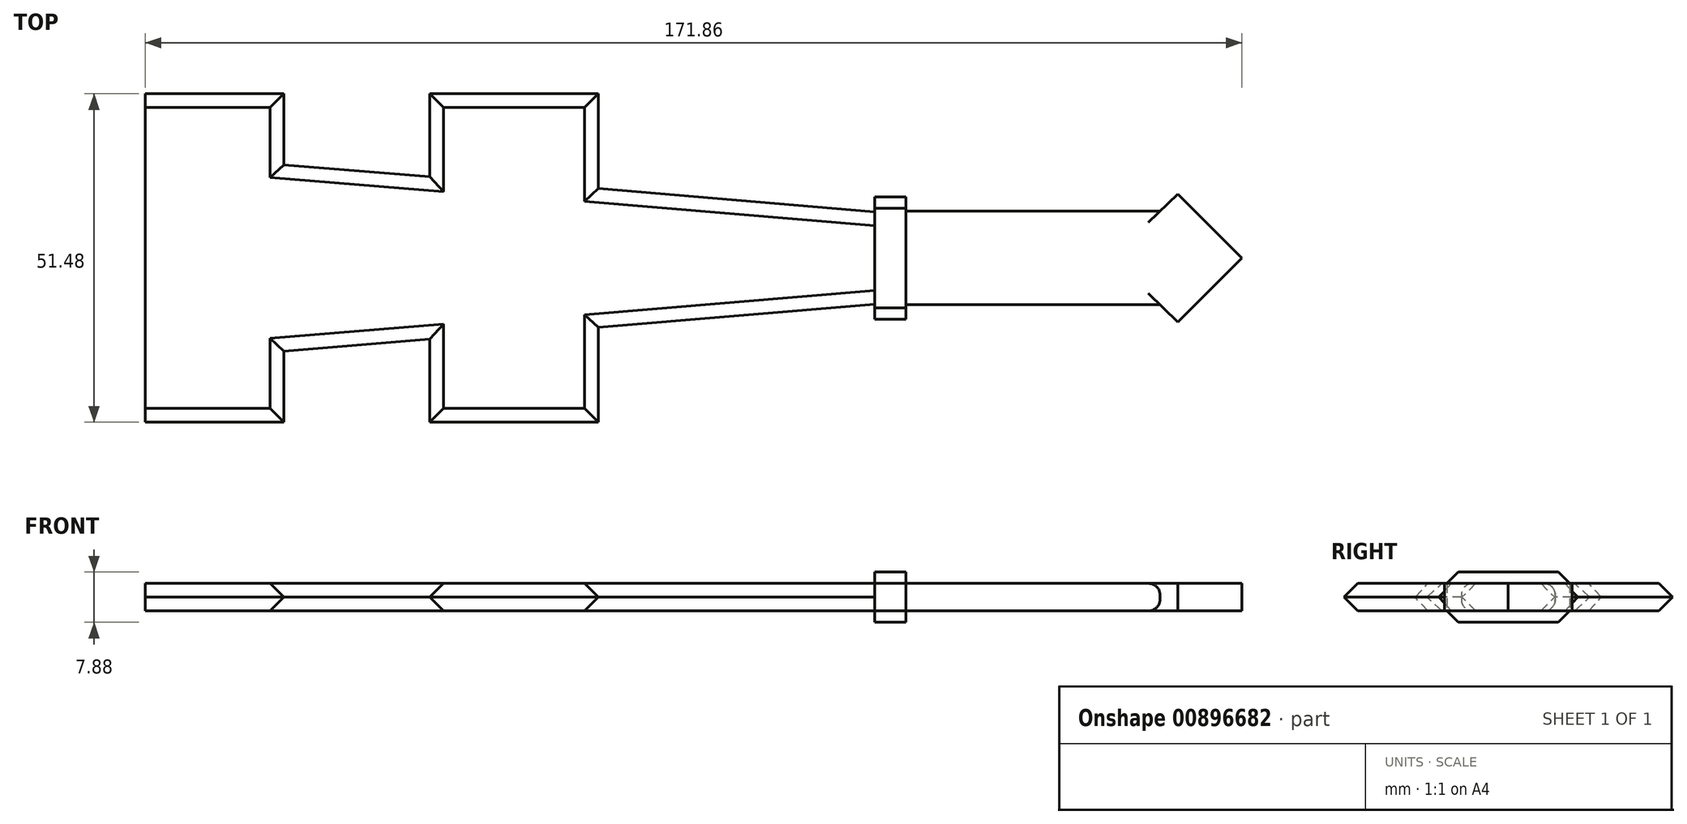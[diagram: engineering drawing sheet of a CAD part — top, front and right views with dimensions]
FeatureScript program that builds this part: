
annotation { "Feature Type Name" : "Feature", "Feature Type Description" : "" }
export const myFeature = defineFeature(function(context is Context, id is Id, definition is map)
    precondition{}
    {
        {
            var Q0;
            Q0=qCreatedBy(makeId("Top.planeOp"),FACE);
            var sketch = newSketch(context, id + "F0", { "sketchPlane" : qUnion([Q0])});
            skLineSegment(sketch, "E0", {"start": v(-86.75, 19.78) * mm, "end": v(-86.75, -31.7) * mm});
            skLineSegment(sketch, "E1", {"start": v(-86.75, -31.7) * mm, "end": v(-64.99, -31.7) * mm});
            skLineSegment(sketch, "E2", {"start": v(-64.99, -31.7) * mm, "end": v(-64.99, -20.56) * mm});
            skLineSegment(sketch, "E3", {"start": v(-64.99, -20.56) * mm, "end": v(-42.16, -18.7) * mm});
            skLineSegment(sketch, "E4", {"start": v(-42.16, -18.7) * mm, "end": v(-42.16, -31.7) * mm});
            skLineSegment(sketch, "E5", {"start": v(-42.16, -31.7) * mm, "end": v(-15.76, -31.7) * mm});
            skLineSegment(sketch, "E6", {"start": v(-15.76, -31.7) * mm, "end": v(-15.76, -16.84) * mm});
            skLineSegment(sketch, "E7", {"start": v(-15.76, -16.84) * mm, "end": v(27.57, -13.22) * mm});
            skLineSegment(sketch, "E8", {"start": v(27.57, -13.22) * mm, "end": v(27.57, -15.56) * mm});
            skLineSegment(sketch, "E9", {"start": v(27.57, -15.56) * mm, "end": v(32.43, -15.56) * mm});
            skLineSegment(sketch, "E10", {"start": v(32.43, -13.32) * mm, "end": v(72.28, -13.32) * mm});
            skLineSegment(sketch, "E11", {"start": v(72.28, -13.32) * mm, "end": v(75.04, -16) * mm});
            skLineSegment(sketch, "E12", {"start": v(85.1, -5.97) * mm, "end": v(75.04, -16) * mm});
            skLineSegment(sketch, "E13.MirrorCS", {"start": v(72.28, 1.38) * mm, "end": v(75.04, 4.06) * mm});
            skLineSegment(sketch, "E14.MirrorCS", {"start": v(27.57, 1.29) * mm, "end": v(27.57, 3.63) * mm});
            skLineSegment(sketch, "E15.MirrorCS", {"start": v(-15.76, 4.9) * mm, "end": v(27.57, 1.29) * mm});
            skLineSegment(sketch, "E16.MirrorCS", {"start": v(32.43, 1.38) * mm, "end": v(72.28, 1.38) * mm});
            skLineSegment(sketch, "E17.MirrorCS", {"start": v(27.57, 3.63) * mm, "end": v(32.43, 3.63) * mm});
            skLineSegment(sketch, "E18.MirrorCS", {"start": v(85.1, -5.97) * mm, "end": v(75.04, 4.06) * mm});
            skLineSegment(sketch, "E19.MirrorCS", {"start": v(-42.16, 6.77) * mm, "end": v(-42.16, 19.77) * mm});
            skLineSegment(sketch, "E20.MirrorCS", {"start": v(-64.99, 8.63) * mm, "end": v(-42.16, 6.77) * mm});
            skLineSegment(sketch, "E21.MirrorCS", {"start": v(-15.76, 19.77) * mm, "end": v(-15.76, 4.9) * mm});
            skLineSegment(sketch, "E22.MirrorCS", {"start": v(-42.16, 19.77) * mm, "end": v(-15.76, 19.77) * mm});
            skLineSegment(sketch, "E23.MirrorCS", {"start": v(-86.75, 19.77) * mm, "end": v(-64.99, 19.77) * mm});
            skLineSegment(sketch, "E24.MirrorCS", {"start": v(-64.99, 19.77) * mm, "end": v(-64.99, 8.63) * mm});
            skLineSegment(sketch, "E25.MirrorCS", {"start": v(-86.75, -31.72) * mm, "end": v(-86.75, 19.77) * mm});
            skLineSegment(sketch, "E26", {"start": v(32.43, -15.56) * mm, "end": v(32.43, -13.32) * mm});
            skLineSegment(sketch, "E27", {"start": v(32.43, 1.38) * mm, "end": v(32.43, 3.63) * mm});
            skLineSegment(sketch, "E28", {"start": v(27.57, 1.29) * mm, "end": v(27.57, -13.22) * mm});
            skLineSegment(sketch, "E29", {"start": v(32.43, -13.32) * mm, "end": v(32.43, 1.38) * mm});
            skSolve(sketch);
        }
        {
            var Q0;
            Q0=qCreatedBy(makeId("Top.planeOp"),FACE);
            var sketch = newSketch(context, id + "F1", { "sketchPlane" : qUnion([Q0])});
            skSolve(sketch);
        }
        {
            var Q0;
            Q0 = qSketchRegion(id + "F1", true);
            var Q1;
            Q1=makeQuery(id+"F0.imprint","IMPRINT",FACE,{"disambiguationData":[TD([[makeQuery(id+"F0.imprint","IMPRINT",EDGE,{"derivedFrom":sQuery(id+"F0.wireOp",EDGE,"E8")}),1.0]])]});
            var Q2;
            Q2=makeQuery(id+"F0.imprint","IMPRINT",FACE,{"disambiguationData":[TD([[makeQuery(id+"F0.imprint","IMPRINT",EDGE,{"derivedFrom":sQuery(id+"F0.wireOp",EDGE,"E10")}),1.0]])]});
            var Q3;
            {var subQ0=sQuery(id+"F0.wireOp",EDGE,"E1");Q3=makeQuery(id+"F0.imprint","IMPRINT",FACE,{"disambiguationData":[TD([[makeQuery(id+"F0.imprint","IMPRINT",EDGE,{"derivedFrom":subQ0}),1.0]])]});}
            extrude(context, id + "F2", {"entities" : qUnion([Q0, Q1, Q2, Q3]), "depth" : 4.32 * mm, "offsetDistance" : 25.4 * mm});
        }
        {
            var Q0;
            Q0=makeQuery(id+"F2.opExtrude","CAP_EDGE",EDGE,{"disambiguationData":[OSD([sQuery(id+"F0.wireOp",EDGE,"E3")])],"isStart":false});
            var Q1;
            Q1=makeQuery(id+"F2.opExtrude","CAP_EDGE",EDGE,{"disambiguationData":[OSD([sQuery(id+"F0.wireOp",EDGE,"E4")])],"isStart":false});
            var Q2;
            Q2=makeQuery(id+"F2.opExtrude","CAP_EDGE",EDGE,{"disambiguationData":[OSD([sQuery(id+"F0.wireOp",EDGE,"E5")])],"isStart":false});
            var Q3;
            Q3=makeQuery(id+"F2.opExtrude","CAP_EDGE",EDGE,{"disambiguationData":[OSD([sQuery(id+"F0.wireOp",EDGE,"E6")])],"isStart":false});
            var Q4;
            Q4=makeQuery(id+"F2.opExtrude","CAP_EDGE",EDGE,{"disambiguationData":[OSD([sQuery(id+"F0.wireOp",EDGE,"E7")])],"isStart":false});
            var Q5;
            Q5=makeQuery(id+"F2.opExtrude","CAP_EDGE",EDGE,{"disambiguationData":[OSD([sQuery(id+"F0.wireOp",EDGE,"E15.MirrorCS")])],"isStart":false});
            var Q6;
            Q6=makeQuery(id+"F2.opExtrude","CAP_EDGE",EDGE,{"disambiguationData":[OSD([sQuery(id+"F0.wireOp",EDGE,"E21.MirrorCS")])],"isStart":false});
            var Q7;
            Q7=makeQuery(id+"F2.opExtrude","CAP_EDGE",EDGE,{"disambiguationData":[OSD([sQuery(id+"F0.wireOp",EDGE,"E22.MirrorCS")])],"isStart":false});
            var Q8;
            Q8=makeQuery(id+"F2.opExtrude","CAP_EDGE",EDGE,{"disambiguationData":[OSD([sQuery(id+"F0.wireOp",EDGE,"E19.MirrorCS")])],"isStart":false});
            var Q9;
            Q9=makeQuery(id+"F2.opExtrude","CAP_EDGE",EDGE,{"disambiguationData":[OSD([sQuery(id+"F0.wireOp",EDGE,"E20.MirrorCS")])],"isStart":false});
            var Q10;
            Q10=makeQuery(id+"F2.opExtrude","CAP_EDGE",EDGE,{"disambiguationData":[OSD([sQuery(id+"F0.wireOp",EDGE,"E24.MirrorCS")])],"isStart":false});
            var Q11;
            Q11=makeQuery(id+"F2.opExtrude","CAP_EDGE",EDGE,{"disambiguationData":[OSD([sQuery(id+"F0.wireOp",EDGE,"E23.MirrorCS")])],"isStart":false});
            var Q12;
            Q12=makeQuery(id+"F2.opExtrude","CAP_EDGE",EDGE,{"disambiguationData":[OSD([sQuery(id+"F0.wireOp",EDGE,"E25.MirrorCS")])],"isStart":false});
            var Q13;
            Q13=makeQuery(id+"F2.opExtrude","CAP_EDGE",EDGE,{"disambiguationData":[OSD([sQuery(id+"F0.wireOp",EDGE,"E1")])],"isStart":false});
            var Q14;
            Q14=makeQuery(id+"F2.opExtrude","CAP_EDGE",EDGE,{"disambiguationData":[OSD([sQuery(id+"F0.wireOp",EDGE,"E2")])],"isStart":false});
            var Q15;
            Q15=makeQuery(id+"F2.opExtrude","CAP_EDGE",EDGE,{"disambiguationData":[OSD([sQuery(id+"F0.wireOp",EDGE,"E5")])],"isStart":true});
            var Q16;
            Q16=makeQuery(id+"F2.opExtrude","CAP_EDGE",EDGE,{"disambiguationData":[OSD([sQuery(id+"F0.wireOp",EDGE,"E6")])],"isStart":true});
            var Q17;
            Q17=makeQuery(id+"F2.opExtrude","CAP_EDGE",EDGE,{"disambiguationData":[OSD([sQuery(id+"F0.wireOp",EDGE,"E7")])],"isStart":true});
            var Q18;
            Q18=makeQuery(id+"F2.opExtrude","CAP_EDGE",EDGE,{"disambiguationData":[OSD([sQuery(id+"F0.wireOp",EDGE,"E4")])],"isStart":true});
            var Q19;
            Q19=makeQuery(id+"F2.opExtrude","CAP_EDGE",EDGE,{"disambiguationData":[OSD([sQuery(id+"F0.wireOp",EDGE,"E3")])],"isStart":true});
            var Q20;
            Q20=makeQuery(id+"F2.opExtrude","CAP_EDGE",EDGE,{"disambiguationData":[OSD([sQuery(id+"F0.wireOp",EDGE,"E1")])],"isStart":true});
            var Q21;
            Q21=makeQuery(id+"F2.opExtrude","CAP_EDGE",EDGE,{"disambiguationData":[OSD([sQuery(id+"F0.wireOp",EDGE,"E2")])],"isStart":true});
            var Q22;
            Q22=makeQuery(id+"F2.opExtrude","CAP_EDGE",EDGE,{"disambiguationData":[OSD([sQuery(id+"F0.wireOp",EDGE,"E25.MirrorCS")])],"isStart":true});
            var Q23;
            Q23=makeQuery(id+"F2.opExtrude","CAP_EDGE",EDGE,{"disambiguationData":[OSD([sQuery(id+"F0.wireOp",EDGE,"E23.MirrorCS")])],"isStart":true});
            var Q24;
            Q24=makeQuery(id+"F2.opExtrude","CAP_EDGE",EDGE,{"disambiguationData":[OSD([sQuery(id+"F0.wireOp",EDGE,"E24.MirrorCS")])],"isStart":true});
            var Q25;
            Q25=makeQuery(id+"F2.opExtrude","CAP_EDGE",EDGE,{"disambiguationData":[OSD([sQuery(id+"F0.wireOp",EDGE,"E20.MirrorCS")])],"isStart":true});
            var Q26;
            Q26=makeQuery(id+"F2.opExtrude","CAP_EDGE",EDGE,{"disambiguationData":[OSD([sQuery(id+"F0.wireOp",EDGE,"E21.MirrorCS")])],"isStart":true});
            var Q27;
            Q27=makeQuery(id+"F2.opExtrude","CAP_EDGE",EDGE,{"disambiguationData":[OSD([sQuery(id+"F0.wireOp",EDGE,"E15.MirrorCS")])],"isStart":true});
            var Q28;
            Q28=makeQuery(id+"F2.opExtrude","CAP_EDGE",EDGE,{"disambiguationData":[OSD([sQuery(id+"F0.wireOp",EDGE,"E19.MirrorCS")])],"isStart":true});
            var Q29;
            Q29=makeQuery(id+"F2.opExtrude","CAP_EDGE",EDGE,{"disambiguationData":[OSD([sQuery(id+"F0.wireOp",EDGE,"E22.MirrorCS")])],"isStart":true});
            chamfer(context, id + "F3", {"entities" : qUnion([Q0, Q1, Q2, Q3, Q4, Q5, Q6, Q7, Q8, Q9, Q10, Q11, Q12, Q13, Q14, Q15, Q16, Q17, Q18, Q19, Q20, Q21, Q22, Q23, Q24, Q25, Q26, Q27, Q28, Q29]), "width" : 2.16 * mm, "tangentPropagation" : true});
        }
        {
            var Q0;
            Q0=makeQuery(id+"F2.opExtrude","CAP_FACE",FACE,{"disambiguationData":[OSD([sQuery(id+"F0.wireOp",EDGE,"E1"),sQuery(id+"F0.wireOp",EDGE,"E2"),sQuery(id+"F0.wireOp",EDGE,"E3"),sQuery(id+"F0.wireOp",EDGE,"E4"),sQuery(id+"F0.wireOp",EDGE,"E5"),sQuery(id+"F0.wireOp",EDGE,"E6"),sQuery(id+"F0.wireOp",EDGE,"E7"),sQuery(id+"F0.wireOp",EDGE,"E8"),sQuery(id+"F0.wireOp",EDGE,"E9"),sQuery(id+"F0.wireOp",EDGE,"E10"),sQuery(id+"F0.wireOp",EDGE,"E11"),sQuery(id+"F0.wireOp",EDGE,"E12"),sQuery(id+"F0.wireOp",EDGE,"E13.MirrorCS"),sQuery(id+"F0.wireOp",EDGE,"E14.MirrorCS"),sQuery(id+"F0.wireOp",EDGE,"E15.MirrorCS"),sQuery(id+"F0.wireOp",EDGE,"E16.MirrorCS"),sQuery(id+"F0.wireOp",EDGE,"E17.MirrorCS"),sQuery(id+"F0.wireOp",EDGE,"E18.MirrorCS"),sQuery(id+"F0.wireOp",EDGE,"E19.MirrorCS"),sQuery(id+"F0.wireOp",EDGE,"E21.MirrorCS"),sQuery(id+"F0.wireOp",EDGE,"E22.MirrorCS"),sQuery(id+"F0.wireOp",EDGE,"E20.MirrorCS"),sQuery(id+"F0.wireOp",EDGE,"E23.MirrorCS"),sQuery(id+"F0.wireOp",EDGE,"E24.MirrorCS"),sQuery(id+"F0.wireOp",EDGE,"E25.MirrorCS"),sQuery(id+"F0.wireOp",EDGE,"E26"),sQuery(id+"F0.wireOp",EDGE,"E27")])],"isStart":false});
            var sketch = newSketch(context, id + "F4", { "sketchPlane" : qUnion([Q0])});
            skLineSegment(sketch, "E30", {"start": v(27.57, 3.63) * mm, "end": v(27.57, -15.56) * mm});
            skLineSegment(sketch, "E31", {"start": v(27.57, -15.56) * mm, "end": v(32.43, -15.56) * mm});
            skLineSegment(sketch, "E32", {"start": v(32.43, -15.56) * mm, "end": v(32.43, 3.63) * mm});
            skLineSegment(sketch, "E33", {"start": v(32.43, 3.63) * mm, "end": v(27.57, 3.63) * mm});
            skSolve(sketch);
        }
        {
            var Q0;
            {var subQ0=sQuery(id+"F4.wireOp",EDGE,"E31");Q0=makeQuery(id+"F4.imprint","IMPRINT",FACE,{"disambiguationData":[TD([[makeQuery(id+"F4.imprint","IMPRINT",EDGE,{"derivedFrom":subQ0}),1.0]])]});}
            extrude(context, id + "F5", {"entities" : qUnion([Q0]), "operationType" : NewBodyOperationType.ADD, "depth" : 1.78 * mm, "offsetDistance" : 25.4 * mm});
        }
        {
            var Q0;
            Q0=makeQuery(id+"F2.opExtrude","CAP_FACE",FACE,{"disambiguationData":[OSD([sQuery(id+"F0.wireOp",EDGE,"E1"),sQuery(id+"F0.wireOp",EDGE,"E2"),sQuery(id+"F0.wireOp",EDGE,"E3"),sQuery(id+"F0.wireOp",EDGE,"E4"),sQuery(id+"F0.wireOp",EDGE,"E5"),sQuery(id+"F0.wireOp",EDGE,"E6"),sQuery(id+"F0.wireOp",EDGE,"E7"),sQuery(id+"F0.wireOp",EDGE,"E8"),sQuery(id+"F0.wireOp",EDGE,"E9"),sQuery(id+"F0.wireOp",EDGE,"E10"),sQuery(id+"F0.wireOp",EDGE,"E11"),sQuery(id+"F0.wireOp",EDGE,"E12"),sQuery(id+"F0.wireOp",EDGE,"E13.MirrorCS"),sQuery(id+"F0.wireOp",EDGE,"E14.MirrorCS"),sQuery(id+"F0.wireOp",EDGE,"E15.MirrorCS"),sQuery(id+"F0.wireOp",EDGE,"E16.MirrorCS"),sQuery(id+"F0.wireOp",EDGE,"E17.MirrorCS"),sQuery(id+"F0.wireOp",EDGE,"E18.MirrorCS"),sQuery(id+"F0.wireOp",EDGE,"E19.MirrorCS"),sQuery(id+"F0.wireOp",EDGE,"E21.MirrorCS"),sQuery(id+"F0.wireOp",EDGE,"E22.MirrorCS"),sQuery(id+"F0.wireOp",EDGE,"E20.MirrorCS"),sQuery(id+"F0.wireOp",EDGE,"E23.MirrorCS"),sQuery(id+"F0.wireOp",EDGE,"E24.MirrorCS"),sQuery(id+"F0.wireOp",EDGE,"E25.MirrorCS"),sQuery(id+"F0.wireOp",EDGE,"E26"),sQuery(id+"F0.wireOp",EDGE,"E27")])],"isStart":true});
            var sketch = newSketch(context, id + "F6", { "sketchPlane" : qUnion([Q0])});
            skLineSegment(sketch, "E34", {"start": v(27.57, 15.56) * mm, "end": v(27.57, -3.63) * mm});
            skLineSegment(sketch, "E35", {"start": v(27.57, -3.63) * mm, "end": v(32.43, -3.63) * mm});
            skLineSegment(sketch, "E36", {"start": v(32.43, -3.63) * mm, "end": v(32.43, 15.56) * mm});
            skLineSegment(sketch, "E37", {"start": v(32.43, 15.56) * mm, "end": v(27.57, 15.56) * mm});
            skSolve(sketch);
        }
        {
            var Q0;
            {var subQ0=sQuery(id+"F6.wireOp",EDGE,"E35");Q0=makeQuery(id+"F6.imprint","IMPRINT",FACE,{"disambiguationData":[TD([[makeQuery(id+"F6.imprint","IMPRINT",EDGE,{"derivedFrom":subQ0}),1.0]])]});}
            extrude(context, id + "F7", {"entities" : qUnion([Q0]), "operationType" : NewBodyOperationType.ADD, "depth" : 1.78 * mm, "offsetDistance" : 25.4 * mm});
        }
        {
            var Q0;
            Q0=makeQuery(id+"F2.opExtrude","CAP_EDGE",EDGE,{"disambiguationData":[OSD([sQuery(id+"F0.wireOp",EDGE,"E16.MirrorCS")])],"isStart":true});
            var Q1;
            Q1=makeQuery(id+"F2.opExtrude","CAP_EDGE",EDGE,{"disambiguationData":[OSD([sQuery(id+"F0.wireOp",EDGE,"E10")])],"isStart":true});
            var Q2;
            Q2=makeQuery(id+"F2.opExtrude","CAP_EDGE",EDGE,{"disambiguationData":[OSD([sQuery(id+"F0.wireOp",EDGE,"E16.MirrorCS")])],"isStart":false});
            var Q3;
            Q3=makeQuery(id+"F2.opExtrude","CAP_EDGE",EDGE,{"disambiguationData":[OSD([sQuery(id+"F0.wireOp",EDGE,"E10")])],"isStart":false});
            fillet(context, id + "F8", {"entities" : qUnion([Q0, Q1, Q2, Q3]), "radius" : 1.78 * mm, "tangentPropagation" : true, "allowEdgeOverflow" : false});
        }
        {
            var Q0;
            Q0=makeQuery(id+"F7.opExtrude","CAP_EDGE",EDGE,{"disambiguationData":[OSD([sQuery(id+"F6.wireOp",EDGE,"E37")])],"isStart":false});
            var Q1;
            Q1=makeQuery(id+"F5.opExtrude","CAP_EDGE",EDGE,{"disambiguationData":[OSD([sQuery(id+"F4.wireOp",EDGE,"E31")])],"isStart":false});
            var Q2;
            Q2=makeQuery(id+"F5.opExtrude","CAP_EDGE",EDGE,{"disambiguationData":[OSD([sQuery(id+"F4.wireOp",EDGE,"E33")])],"isStart":false});
            var Q3;
            Q3=makeQuery(id+"F7.opExtrude","CAP_EDGE",EDGE,{"disambiguationData":[OSD([sQuery(id+"F6.wireOp",EDGE,"E35")])],"isStart":false});
            chamfer(context, id + "F9", {"entities" : qUnion([Q0, Q1, Q2, Q3]), "width" : 1.78 * mm, "tangentPropagation" : true});
        }
    });
